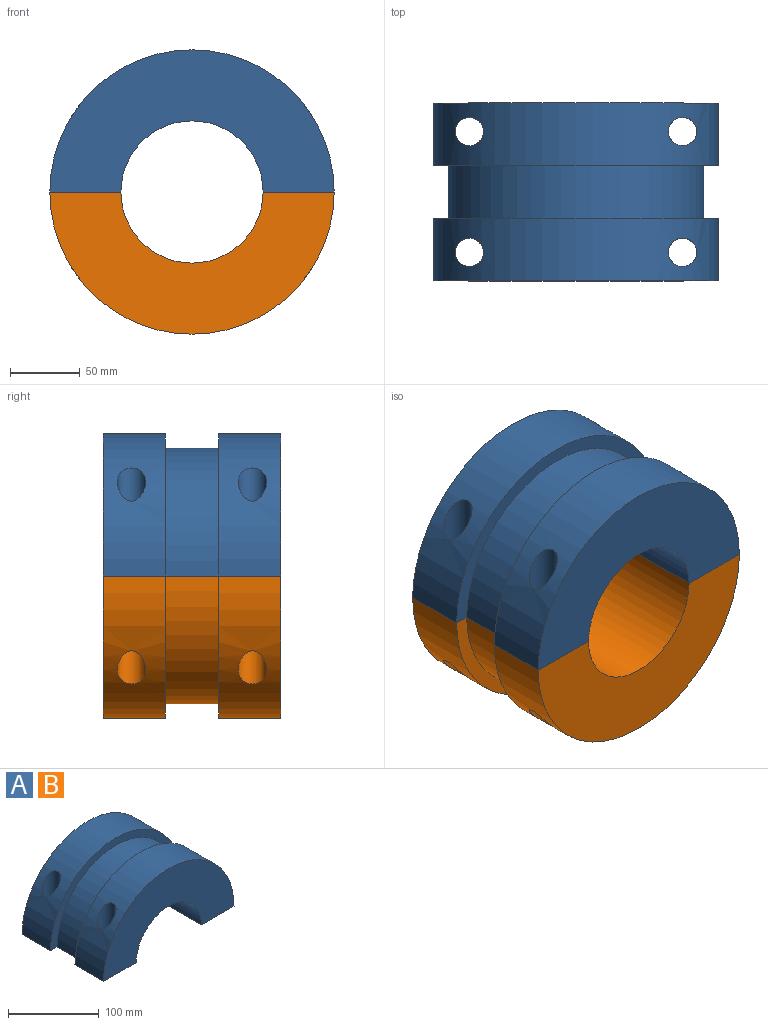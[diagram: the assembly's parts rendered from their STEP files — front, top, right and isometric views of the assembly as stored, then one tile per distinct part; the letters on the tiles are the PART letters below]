
ASSEMBLY  parts=2 mates=1
PART A: 14 faces, bbox 203.2x127x101.6 mm
  f0: cylinder r=101.6mm len=203.2mm, axis (0,1,0), area 13182.5mm2, adj f1,f4,f6,f7,f10,f11
  f1: plane 127x50.8mm, normal (0,0,-1), area 5415.9mm2, adj f0,f2,f3,f5,f6,f9,f10,f11
  f2: cylinder r=101.6mm len=203.2mm, axis (0,1,0), area 13182.5mm2, adj f1,f4,f5,f8,f9,f12
  f3: cylinder r=50.8mm len=127mm, axis (0,1,0), area 20268.3mm2, adj f1,f4,f5,f6
  f4: plane 127x50.8mm, normal (0,0,-1), area 5415.9mm2, adj f0,f2,f3,f5,f6,f7,f8,f11
  f5: plane 203.2x101.6mm, normal (0,-1,0), area 12161mm2, adj f1,f2,f3,f4
  f6: plane 203.2x101.6mm, normal (0,1,0), area 12161mm2, adj f0,f1,f3,f4
  f7: cylinder r=10.16mm len=77.21mm, axis (0,0,-1), area 4231.9mm2, adj f0,f4
  f8: cylinder r=10.16mm len=77.21mm, axis (0,0,-1), area 4231.9mm2, adj f2,f4
  f9: cylinder r=10.16mm len=77.21mm, axis (0,0,-1), area 4232.1mm2, adj f1,f2
  f10: cylinder r=10.16mm len=77.21mm, axis (0,0,-1), area 4232.1mm2, adj f0,f1
  f11: plane 203.2x101.6mm, normal (0,-1,0), area 3080.8mm2, adj f0,f1,f4,f13
  f12: plane 203.2x101.6mm, normal (0,1,0), area 3080.8mm2, adj f1,f2,f4,f13
  f13: cylinder r=91.44mm len=182.88mm, axis (0,-1,0), area 10944.9mm2, adj f1,f4,f11,f12
PART B: same geometry as A
PLACE A t=(101.25,-72.78,145.56)mm
PLACE B rot(axis=(1,0,0),180deg) t=(101.25,-72.78,145.56)mm
MATE planar A.f4 <-> B.f4  axis (0,0,-1) through (175.99,-72.78,145.56)mm
